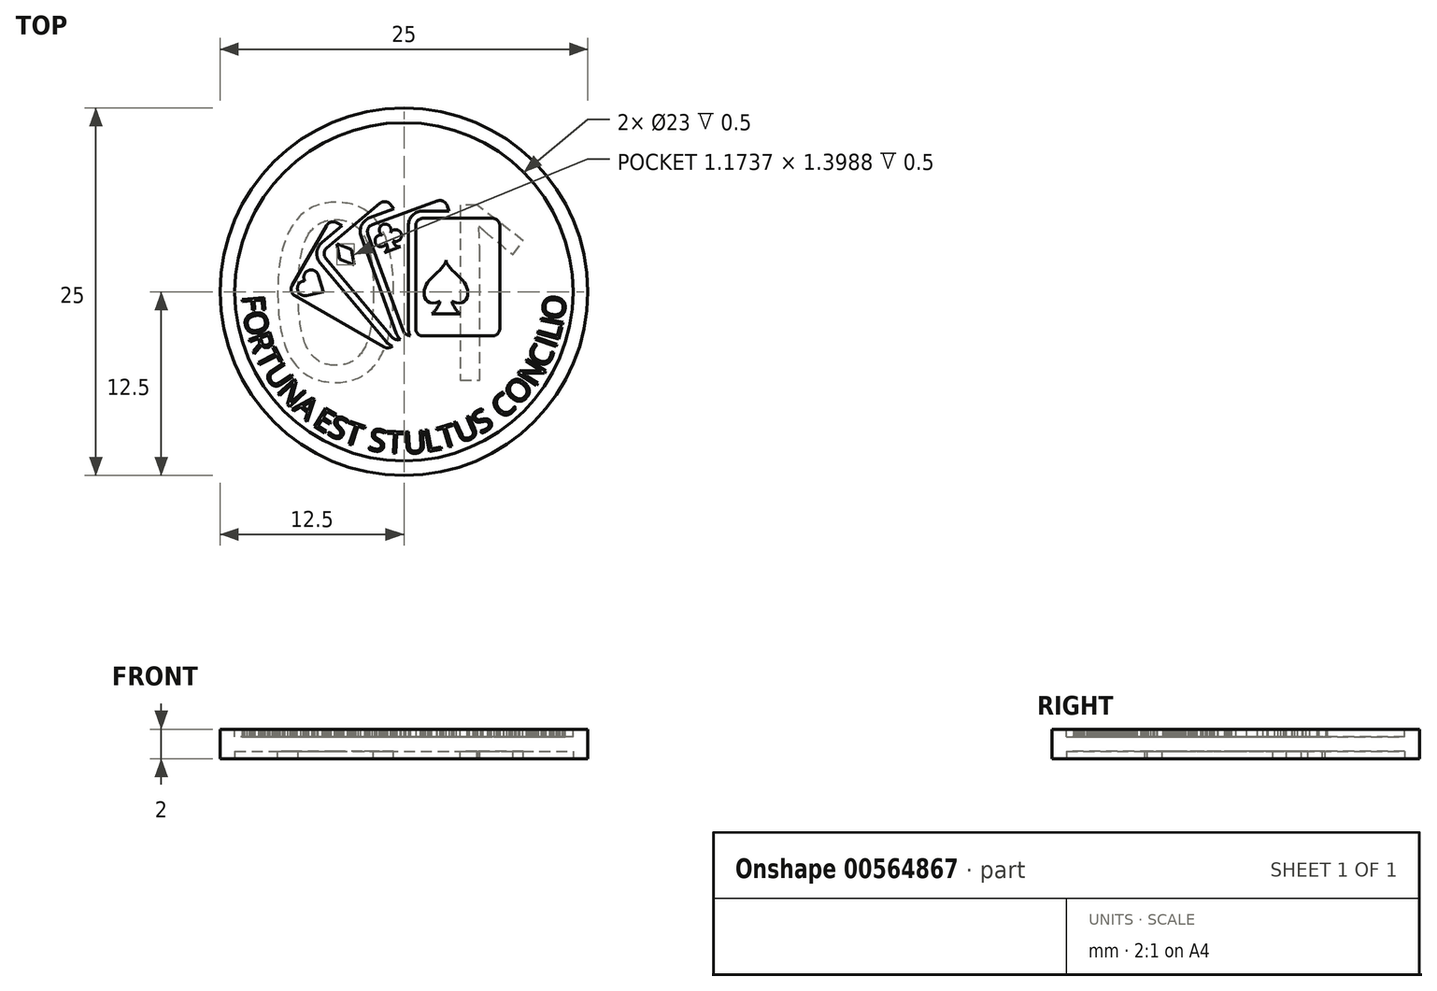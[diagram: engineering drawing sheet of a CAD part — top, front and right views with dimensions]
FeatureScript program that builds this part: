
annotation { "Feature Type Name" : "Feature", "Feature Type Description" : "" }
export const myFeature = defineFeature(function(context is Context, id is Id, definition is map)
    precondition{}
    {
        {
            assignVariable(context, id + "F0", {"name" : "ImpressionDepth", "anyValue" : 0.5});
        }
        {
            var Q0;
            Q0=qCreatedBy(makeId("Top.planeOp"),FACE);
            var sketch = newSketch(context, id + "F1", { "sketchPlane" : qUnion([Q0])});
            skCircle(sketch, "E0", {"center": v(0, 0) * mm, "radius": 12.5 * mm});
            skSolve(sketch);
        }
        {
            var Q0;
            Q0=qSketchRegion(id+"F1",true);
            extrude(context, id + "F2", {"entities" : qUnion([Q0]), "depth" : 2 * mm});
        }
        {
            var Q0;
            Q0=makeQuery(id+"F2.opExtrude","CAP_FACE",FACE,{"disambiguationData":[OSD([sQuery(id+"F1.wireOp",EDGE,"E0")])],"isStart":false});
            var sketch = newSketch(context, id + "F3", { "sketchPlane" : qUnion([Q0])});
            skCircle(sketch, "E1.0", {"center": v(0, 0) * mm, "radius": 11.5 * mm});
            skSolve(sketch);
        }
        {
            var Q0;
            Q0=qSketchRegion(id+"F3",true);
            extrude(context, id + "F4", {"entities" : qUnion([Q0]), "operationType" : NewBodyOperationType.REMOVE, "oppositeDirection" : true, "depth" : (getVariable(context, 'ImpressionDepth')) * mm});
        }
        {
            var Q0;
            Q0=makeQuery(id+"F2.opExtrude","CAP_FACE",FACE,{"disambiguationData":[OSD([sQuery(id+"F1.wireOp",EDGE,"E0")])],"isStart":true});
            var sketch = newSketch(context, id + "F5", { "sketchPlane" : qUnion([Q0])});
            skCircle(sketch, "E2.0", {"center": v(0, 0) * mm, "radius": 11.5 * mm});
            skSolve(sketch);
        }
        {
            var Q0;
            Q0=qSketchRegion(id+"F5",true);
            extrude(context, id + "F6", {"entities" : qUnion([Q0]), "operationType" : NewBodyOperationType.REMOVE, "oppositeDirection" : true, "depth" : (getVariable(context, 'ImpressionDepth')) * mm});
        }
        {
            var Q0;
            Q0=makeQuery(id+"F6.boolean.opBoolean","COPY",FACE,{"derivedFrom":makeQuery(id+"F6.opExtrude","CAP_FACE",FACE,{"disambiguationData":[OSD([sQuery(id+"F5.wireOp",EDGE,"E2.0")])],"isStart":false})});
            var sketch = newSketch(context, id + "F7", { "sketchPlane" : qUnion([Q0])});
            skText(sketch, "E3", { "text": "10", "fontName": "OpenSans-Regular.ttf"});
            skPoint(sketch, "E4", {"position": v(0, 0) * mm});
            const initialGuessF7  = {"E3": [0.00965, 0.006, -1, 0, 0.012]};
            skSetInitialGuess(sketch, initialGuessF7);
            skSolve(sketch);
        }
        {
            var Q0;
            Q0=qSketchRegion(id+"F7",true);
            extrude(context, id + "F8", {"entities" : qUnion([Q0]), "operationType" : NewBodyOperationType.ADD, "depth" : (getVariable(context, 'ImpressionDepth')) * mm});
        }
        {
            var Q0;
            Q0=makeQuery(id+"F4.boolean.opBoolean","COPY",FACE,{"derivedFrom":makeQuery(id+"F4.opExtrude","CAP_FACE",FACE,{"disambiguationData":[OSD([sQuery(id+"F3.wireOp",EDGE,"E1.0")])],"isStart":false})});
            var sketch = newSketch(context, id + "F9", { "sketchPlane" : qUnion([Q0])});
            skLineSegment(sketch, "E5.bottom", {"start": v(1.3, 5) * mm, "end": v(6.01, 5) * mm});
            skLineSegment(sketch, "E5.top", {"start": v(1.3, -3) * mm, "end": v(6.01, -3) * mm});
            skLineSegment(sketch, "E5.left", {"start": v(0.8, 4.5) * mm, "end": v(0.8, -2.5) * mm});
            skLineSegment(sketch, "E5.right", {"start": v(6.51, 4.5) * mm, "end": v(6.51, -2.5) * mm});
            skPoint(sketch, "E6.visualSharp", {"position": v(0.8, 5) * mm});
            skArc(sketch, "E6.filletArc", {"start": v(1.3, 5) * mm, "mid": v(0.95, 4.85) * mm, "end": v(0.8, 4.5) * mm});
            skPoint(sketch, "E7.visualSharp", {"position": v(6.51, 5) * mm});
            skArc(sketch, "E7.filletArc", {"start": v(6.51, 4.5) * mm, "mid": v(6.37, 4.85) * mm, "end": v(6.01, 5) * mm});
            skPoint(sketch, "E8.visualSharp", {"position": v(0.8, -3) * mm});
            skArc(sketch, "E8.filletArc", {"start": v(0.8, -2.5) * mm, "mid": v(0.95, -2.85) * mm, "end": v(1.3, -3) * mm});
            skPoint(sketch, "E9.visualSharp", {"position": v(6.51, -3) * mm});
            skArc(sketch, "E9.filletArc", {"start": v(6.01, -3) * mm, "mid": v(6.37, -2.85) * mm, "end": v(6.51, -2.5) * mm});
            skPoint(sketch, "E10", {"position": v(0.8, -5) * mm});
            skLineSegment(sketch, "E11.bottom", {"start": v(-2.15, 4.57) * mm, "end": v(2.28, 6.18) * mm});
            skLineSegment(sketch, "E11.left", {"start": v(-2.45, 3.93) * mm, "end": v(-0.06, -2.65) * mm});
            skLineSegment(sketch, "E11.right", {"start": v(2.92, 5.88) * mm, "end": v(3.06, 5.5) * mm});
            skPoint(sketch, "E12.visualSharp", {"position": v(-2.62, 4.4) * mm});
            skArc(sketch, "E12.filletArc", {"start": v(-2.15, 4.57) * mm, "mid": v(-2.43, 4.3) * mm, "end": v(-2.45, 3.93) * mm});
            skPoint(sketch, "E13.visualSharp", {"position": v(2.75, 6.35) * mm});
            skArc(sketch, "E13.filletArc", {"start": v(2.92, 5.88) * mm, "mid": v(2.66, 6.16) * mm, "end": v(2.28, 6.18) * mm});
            skPoint(sketch, "E14.visualSharp", {"position": v(0.12, -3.12) * mm});
            skArc(sketch, "E14.filletArc", {"start": v(-0.06, -2.65) * mm, "mid": v(0.13, -2.9) * mm, "end": v(0.42, -2.98) * mm});
            skLineSegment(sketch, "E15", {"start": v(0.8, -5) * mm, "end": v(-2.62, 4.4) * mm, "construction": true});
            skLineSegment(sketch, "E16", {"start": v(0.8, -3) * mm, "end": v(0.8, -5) * mm, "construction": true});
            skLineSegment(sketch, "E17", {"start": v(1.3, 5) * mm, "end": v(3.24, 5) * mm});
            skArc(sketch, "E18.0", {"start": v(0.3, -2.5) * mm, "mid": v(0.33, -2.75) * mm, "end": v(0.42, -2.98) * mm});
            skLineSegment(sketch, "E18.1", {"start": v(0.3, 4.5) * mm, "end": v(0.3, -2.5) * mm});
            skArc(sketch, "E18.2", {"start": v(1.3, 5.5) * mm, "mid": v(0.6, 5.2) * mm, "end": v(0.3, 4.5) * mm});
            skLineSegment(sketch, "E18.3", {"start": v(1.3, 5.5) * mm, "end": v(3.06, 5.5) * mm});
            skLineSegment(sketch, "E19", {"start": v(-0.06, -2.65) * mm, "end": v(0.41, -2.48) * mm, "construction": true});
            skLineSegment(sketch, "E20", {"start": v(0.42, -2.98) * mm, "end": v(0.41, -2.48) * mm, "construction": true});
            skLineSegment(sketch, "E21.bottom", {"start": v(-5.24, 2.98) * mm, "end": v(-1.63, 6.01) * mm});
            skLineSegment(sketch, "E21.left", {"start": v(-5.3, 2.28) * mm, "end": v(-0.8, -3.08) * mm});
            skLineSegment(sketch, "E21.right", {"start": v(-0.93, 5.95) * mm, "end": v(-0.67, 5.64) * mm});
            skPoint(sketch, "E22.visualSharp", {"position": v(-5.63, 2.66) * mm});
            skArc(sketch, "E22.filletArc", {"start": v(-5.24, 2.98) * mm, "mid": v(-5.42, 2.64) * mm, "end": v(-5.3, 2.28) * mm});
            skPoint(sketch, "E23.visualSharp", {"position": v(-1.25, 6.33) * mm});
            skArc(sketch, "E23.filletArc", {"start": v(-0.93, 5.95) * mm, "mid": v(-1.27, 6.13) * mm, "end": v(-1.63, 6.01) * mm});
            skPoint(sketch, "E24.visualSharp", {"position": v(-0.49, -3.47) * mm});
            skArc(sketch, "E24.filletArc", {"start": v(-0.8, -3.08) * mm, "mid": v(-0.55, -3.25) * mm, "end": v(-0.25, -3.23) * mm});
            skLineSegment(sketch, "E25", {"start": v(-0.49, -3.47) * mm, "end": v(0.8, -5) * mm, "construction": true});
            skLineSegment(sketch, "E26", {"start": v(-5.24, 2.98) * mm, "end": v(-2.54, 5.26) * mm});
            skArc(sketch, "E27.0", {"start": v(-0.52, -2.82) * mm, "mid": v(-0.41, -3.04) * mm, "end": v(-0.25, -3.23) * mm});
            skLineSegment(sketch, "E27.1", {"start": v(-2.92, 3.76) * mm, "end": v(-0.52, -2.82) * mm});
            skArc(sketch, "E27.2", {"start": v(-2.32, 5.04) * mm, "mid": v(-2.89, 4.52) * mm, "end": v(-2.92, 3.76) * mm});
            skLineSegment(sketch, "E27.3", {"start": v(-2.32, 5.04) * mm, "end": v(-0.67, 5.64) * mm});
            skLineSegment(sketch, "E28", {"start": v(-0.8, -3.08) * mm, "end": v(-0.42, -2.76) * mm, "construction": true});
            skLineSegment(sketch, "E29", {"start": v(-0.25, -3.23) * mm, "end": v(-0.42, -2.76) * mm, "construction": true});
            skLineSegment(sketch, "E30.bottom", {"start": v(-7.61, 0.43) * mm, "end": v(-5.25, 4.52) * mm});
            skLineSegment(sketch, "E30.top", {"start": v(-0.4, -3.07) * mm, "end": v(-0.34, -2.98) * mm});
            skLineSegment(sketch, "E30.left", {"start": v(-7.43, -0.25) * mm, "end": v(-1.37, -3.75) * mm});
            skLineSegment(sketch, "E30.right", {"start": v(-4.57, 4.7) * mm, "end": v(-4.22, 4.5) * mm});
            skPoint(sketch, "E31.visualSharp", {"position": v(-7.86, 0) * mm});
            skArc(sketch, "E31.filletArc", {"start": v(-7.61, 0.43) * mm, "mid": v(-7.66, 0.05) * mm, "end": v(-7.43, -0.25) * mm});
            skPoint(sketch, "E32.visualSharp", {"position": v(-5, 4.95) * mm});
            skArc(sketch, "E32.filletArc", {"start": v(-4.57, 4.7) * mm, "mid": v(-4.95, 4.75) * mm, "end": v(-5.25, 4.52) * mm});
            skPoint(sketch, "E33.visualSharp", {"position": v(-0.93, -4) * mm});
            skArc(sketch, "E33.filletArc", {"start": v(-1.37, -3.75) * mm, "mid": v(-1.07, -3.81) * mm, "end": v(-0.79, -3.7) * mm});
            skPoint(sketch, "E34.visualSharp", {"position": v(1.93, 0.95) * mm});
            skLineSegment(sketch, "E35", {"start": v(-0.93, -4) * mm, "end": v(0.8, -5) * mm, "construction": true});
            skLineSegment(sketch, "E36", {"start": v(-7.61, 0.43) * mm, "end": v(-5.67, 3.8) * mm});
            skLineSegment(sketch, "E37.0", {"start": v(-5.57, 3.36) * mm, "end": v(-4.22, 4.5) * mm});
            skArc(sketch, "E37.1", {"start": v(-5.57, 3.36) * mm, "mid": v(-5.92, 2.69) * mm, "end": v(-5.69, 1.96) * mm});
            skLineSegment(sketch, "E37.2", {"start": v(-5.69, 1.96) * mm, "end": v(-1.19, -3.4) * mm});
            skArc(sketch, "E37.3", {"start": v(-1.19, -3.4) * mm, "mid": v(-1, -3.58) * mm, "end": v(-0.79, -3.7) * mm});
            skSolve(sketch);
        }
        {
            var Q0;
            Q0=qSketchRegion(id+"F9",true);
            extrude(context, id + "F10", {"entities" : qUnion([Q0]), "operationType" : NewBodyOperationType.ADD, "depth" : (getVariable(context, 'ImpressionDepth')) * mm});
        }
        {
            var Q0;
            Q0=makeQuery(id+"F10.opExtrude","CAP_FACE",FACE,{"disambiguationData":[OSD([sQuery(id+"F9.wireOp",EDGE,"E5.bottom"),sQuery(id+"F9.wireOp",EDGE,"E5.top"),sQuery(id+"F9.wireOp",EDGE,"E5.right"),sQuery(id+"F9.wireOp",EDGE,"E6.filletArc"),sQuery(id+"F9.wireOp",EDGE,"E7.filletArc"),sQuery(id+"F9.wireOp",EDGE,"E8.filletArc"),sQuery(id+"F9.wireOp",EDGE,"E9.filletArc"),sQuery(id+"F9.wireOp",EDGE,"E17"),sQuery(id+"F9.wireOp",EDGE,"E5.left")])],"isStart":false});
            var sketch = newSketch(context, id + "F11", { "sketchPlane" : qUnion([Q0])});
            skLineSegment(sketch, "E38", {"start": v(2.86, 5) * mm, "end": v(2.86, -3) * mm, "construction": true});
            skLineSegment(sketch, "E39", {"start": v(0.8, 0) * mm, "end": v(6.51, 0) * mm, "construction": true});
            skLineSegment(sketch, "E40", {"start": v(2.86, -1.5) * mm, "end": v(3.82, -1.5) * mm});
            skPoint(sketch, "E41", {"position": v(3.26, -0.64) * mm});
            skPoint(sketch, "E42", {"position": v(4.73, -0.3) * mm});
            skArc(sketch, "E43", {"start": v(3.26, -0.64) * mm, "mid": v(3.46, -1.12) * mm, "end": v(3.82, -1.5) * mm});
            skPoint(sketch, "E44", {"position": v(2.86, 2.16) * mm});
            skPoint(sketch, "E45", {"position": v(3.36, 1.4) * mm});
            skPoint(sketch, "E46", {"position": v(4.16, 0.53) * mm});
            skFitSpline(sketch, "E47", {"points": [v(3.26, -0.64) * mm, v(4.29, -0.43) * mm, v(4.16, 0.53) * mm, v(3.36, 1.4) * mm, v(2.86, 2.16) * mm], "startDerivative": vector(6.48, -2.91) * mm, "endDerivative": vector(0, 2.74) * mm});
            skFitSpline(sketch, "E48.MirrorCS", {"points": [v(2.46, -0.64) * mm, v(1.43, -0.43) * mm, v(1.56, 0.53) * mm, v(2.36, 1.4) * mm, v(2.86, 2.16) * mm], "startDerivative": vector(-6.48, -2.91) * mm, "endDerivative": vector(0, 2.74) * mm});
            skArc(sketch, "E49.MirrorCS", {"start": v(2.46, -0.64) * mm, "mid": v(2.25, -1.12) * mm, "end": v(1.9, -1.5) * mm});
            skLineSegment(sketch, "E50.MirrorCS", {"start": v(2.86, -1.5) * mm, "end": v(1.9, -1.5) * mm});
            skLineSegment(sketch, "E51", {"start": v(-2.14, 3.08) * mm, "end": v(-1.01, 3.5) * mm, "construction": true});
            skLineSegment(sketch, "E52", {"start": v(-1.01, 3.5) * mm, "end": v(-1.5, 4.8) * mm, "construction": true});
            skLineSegment(sketch, "E53", {"start": v(-1.01, 3.5) * mm, "end": v(-0.53, 2.18) * mm, "construction": true});
            skLineSegment(sketch, "E54", {"start": v(-0.79, 2.87) * mm, "end": v(-0.25, 3.06) * mm});
            skPoint(sketch, "E55", {"position": v(-0.73, 3.46) * mm});
            skPoint(sketch, "E56", {"position": v(-1.27, 4.2) * mm});
            skPoint(sketch, "E57", {"position": v(-0.57, 3.83) * mm});
            skPoint(sketch, "E58", {"position": v(-0.29, 3.5) * mm});
            skArc(sketch, "E59", {"start": v(-0.73, 3.46) * mm, "mid": v(-0.57, 3.16) * mm, "end": v(-0.25, 3.06) * mm});
            skArc(sketch, "E60", {"start": v(-0.73, 3.46) * mm, "mid": v(-0.19, 3.95) * mm, "end": v(-0.91, 4.04) * mm});
            skArc(sketch, "E61", {"start": v(-1.41, 4.58) * mm, "mid": v(-0.98, 4.48) * mm, "end": v(-0.91, 4.04) * mm});
            skArc(sketch, "E62.MirrorCS", {"start": v(-1.41, 4.58) * mm, "mid": v(-1.67, 4.22) * mm, "end": v(-1.44, 3.84) * mm});
            skArc(sketch, "E63.MirrorCS", {"start": v(-1.2, 3.29) * mm, "mid": v(-1.94, 3.3) * mm, "end": v(-1.44, 3.84) * mm});
            skArc(sketch, "E64.MirrorCS", {"start": v(-1.2, 3.29) * mm, "mid": v(-1.14, 2.96) * mm, "end": v(-1.32, 2.67) * mm});
            skLineSegment(sketch, "E65.MirrorCS", {"start": v(-0.79, 2.87) * mm, "end": v(-1.32, 2.67) * mm});
            skLineSegment(sketch, "E66", {"start": v(-4.89, 1.78) * mm, "end": v(-3.97, 2.55) * mm, "construction": true});
            skLineSegment(sketch, "E67", {"start": v(-3.97, 2.55) * mm, "end": v(-4.7, 3.43) * mm, "construction": true});
            skLineSegment(sketch, "E68", {"start": v(-4.35, 2.23) * mm, "end": v(-4.55, 3.25) * mm});
            skLineSegment(sketch, "E69", {"start": v(-3.97, 2.55) * mm, "end": v(-3.38, 1.85) * mm, "construction": true});
            skLineSegment(sketch, "E70", {"start": v(-4.35, 2.23) * mm, "end": v(-3.38, 1.85) * mm});
            skLineSegment(sketch, "E71.MirrorCS", {"start": v(-3.58, 2.87) * mm, "end": v(-4.55, 3.25) * mm});
            skLineSegment(sketch, "E72.MirrorCS", {"start": v(-3.58, 2.87) * mm, "end": v(-3.38, 1.85) * mm});
            skLineSegment(sketch, "E73", {"start": v(-6.86, -0.58) * mm, "end": v(-6.26, 0.46) * mm, "construction": true});
            skLineSegment(sketch, "E74", {"start": v(-6.26, 0.46) * mm, "end": v(-7.26, 1.04) * mm, "construction": true});
            skLineSegment(sketch, "E75", {"start": v(-6.26, 0.46) * mm, "end": v(-5.47, 0) * mm, "construction": true});
            skLineSegment(sketch, "E76", {"start": v(-5.47, 0) * mm, "end": v(-5.83, 1.14) * mm});
            skArc(sketch, "E77", {"start": v(-5.83, 1.14) * mm, "mid": v(-6.5, 1.45) * mm, "end": v(-6.74, 0.74) * mm});
            skArc(sketch, "E78.MirrorCS", {"start": v(-6.63, -0.25) * mm, "mid": v(-7.24, 0.19) * mm, "end": v(-6.74, 0.74) * mm});
            skLineSegment(sketch, "E79.MirrorCS", {"start": v(-5.47, 0) * mm, "end": v(-6.63, -0.25) * mm});
            skSolve(sketch);
        }
        {
            var Q0;
            Q0=qSketchRegion(id+"F11",true);
            extrude(context, id + "F12", {"entities" : qUnion([Q0]), "operationType" : NewBodyOperationType.REMOVE, "oppositeDirection" : true, "depth" : (getVariable(context, 'ImpressionDepth')) * mm});
        }
        {
            var Q0;
            Q0=makeQuery(id+"F4.boolean.opBoolean","COPY",FACE,{"derivedFrom":makeQuery(id+"F4.opExtrude","CAP_FACE",FACE,{"disambiguationData":[OSD([sQuery(id+"F3.wireOp",EDGE,"E1.0")])],"isStart":false})});
            var sketch = newSketch(context, id + "F13", { "sketchPlane" : qUnion([Q0])});
            skCircle(sketch, "E80", {"center": v(0, 0) * mm, "radius": 11 * mm, "construction": true});
            skLineSegment(sketch, "E81", {"start": v(0, 0) * mm, "end": v(0, -11) * mm, "construction": true});
            skText(sketch, "E82", { "text": "U", "fontName": "OpenSans-Regular.ttf"});
            skText(sketch, "E83", { "text": "L\n", "fontName": "OpenSans-Regular.ttf"});
            skText(sketch, "E84", { "text": "T", "fontName": "OpenSans-Regular.ttf"});
            skText(sketch, "E85", { "text": "U", "fontName": "OpenSans-Regular.ttf"});
            skText(sketch, "E86", { "text": "S", "fontName": "OpenSans-Regular.ttf"});
            skText(sketch, "E87", { "text": "C", "fontName": "OpenSans-Regular.ttf"});
            skText(sketch, "E88", { "text": "O", "fontName": "OpenSans-Regular.ttf"});
            skText(sketch, "E89", { "text": "N", "fontName": "OpenSans-Regular.ttf"});
            skText(sketch, "E90", { "text": "C", "fontName": "OpenSans-Regular.ttf"});
            skText(sketch, "E91", { "text": "O", "fontName": "OpenSans-Regular.ttf"});
            skText(sketch, "E92", { "text": "I", "fontName": "OpenSans-Regular.ttf"});
            skText(sketch, "E93", { "text": "L", "fontName": "OpenSans-Regular.ttf"});
            skText(sketch, "E94", { "text": "I", "fontName": "OpenSans-Regular.ttf"});
            skText(sketch, "E95", { "text": "F", "fontName": "OpenSans-Regular.ttf"});
            skText(sketch, "E96", { "text": "O", "fontName": "OpenSans-Regular.ttf"});
            skText(sketch, "E97", { "text": "R", "fontName": "OpenSans-Regular.ttf"});
            skText(sketch, "E98", { "text": "T", "fontName": "OpenSans-Regular.ttf"});
            skText(sketch, "E99", { "text": "U", "fontName": "OpenSans-Regular.ttf"});
            skText(sketch, "E100", { "text": "N", "fontName": "OpenSans-Regular.ttf"});
            skText(sketch, "E101", { "text": "A", "fontName": "OpenSans-Regular.ttf"});
            skText(sketch, "E102", { "text": "E", "fontName": "OpenSans-Regular.ttf"});
            skText(sketch, "E103", { "text": "S", "fontName": "OpenSans-Regular.ttf"});
            skText(sketch, "E104", { "text": "T", "fontName": "OpenSans-Regular.ttf"});
            skText(sketch, "E105", { "text": "S", "fontName": "OpenSans-Regular.ttf"});
            skText(sketch, "E106", { "text": "T", "fontName": "OpenSans-Regular.ttf"});
            const initialGuessF13  = {"E82": [4e-05, -0.01102, 0.99756, 0.06976, 0.0015], "E83": [0.00153, -0.0109, 0.98163, 0.1908, 0.0015], "E84": [0.00261, -0.0107, 0.95629, 0.29243, 0.0015], "E85": [0.00382, -0.01034, 0.9129, 0.40819, 0.0015], "E86": [0.00521, -0.0097, 0.85425, 0.51986, 0.0015], "E87": [0.00674, -0.00872, 0.751, 0.6603, 0.0015], "E88": [0.0078, -0.0078, 0.65346, 0.75696, 0.0015], "E89": [0.0089, -0.00652, 0.5351, 0.8448, 0.0015], "E90": [0.0097, -0.00525, 0.41965, 0.90769, 0.0015], "E91": [0.01086, -0.00193, 0.10138, 0.99485, 0.0015], "E92": [0.01028, -0.00393, 0.33522, 0.94214, 0.0015], "E93": [0.01048, -0.0034, 0.25807, 0.96613, 0.0015], "E94": [0.01073, -0.00244, 0.1986, 0.98008, 0.0015], "E95": [-0.01101, -0.0003, 0.07969, -0.99682, 0.0015], "E96": [-0.01093, -0.00148, 0.20736, -0.97826, 0.0015], "E97": [-0.0106, -0.00305, 0.33662, -0.94164, 0.0015], "E98": [-0.01012, -0.00436, 0.4478, -0.89413, 0.0015], "E99": [-0.00955, -0.0055, 0.55578, -0.83133, 0.0015], "E100": [-0.00869, -0.00679, 0.66797, -0.74419, 0.0015], "E101": [-0.0076, -0.00799, 0.76846, -0.6399, 0.0015], "E102": [-0.00626, -0.00906, 0.8518, -0.52386, 0.0015], "E103": [-0.00527, -0.00967, 0.90245, -0.43079, 0.0015], "E104": [-0.00418, -0.0102, 0.94569, -0.32507, 0.0015], "E105": [-0.00247, -0.01073, 0.98509, -0.17205, 0.0015], "E106": [-0.00121, -0.01095, 0.9986, -0.05274, 0.0015]};
            skSetInitialGuess(sketch, initialGuessF13);
            skSolve(sketch);
        }
        {
            var Q0;
            Q0=qSketchRegion(id+"F13",true);
            extrude(context, id + "F14", {"entities" : qUnion([Q0]), "operationType" : NewBodyOperationType.ADD, "depth" : (getVariable(context, 'ImpressionDepth')) * mm});
        }
    });
